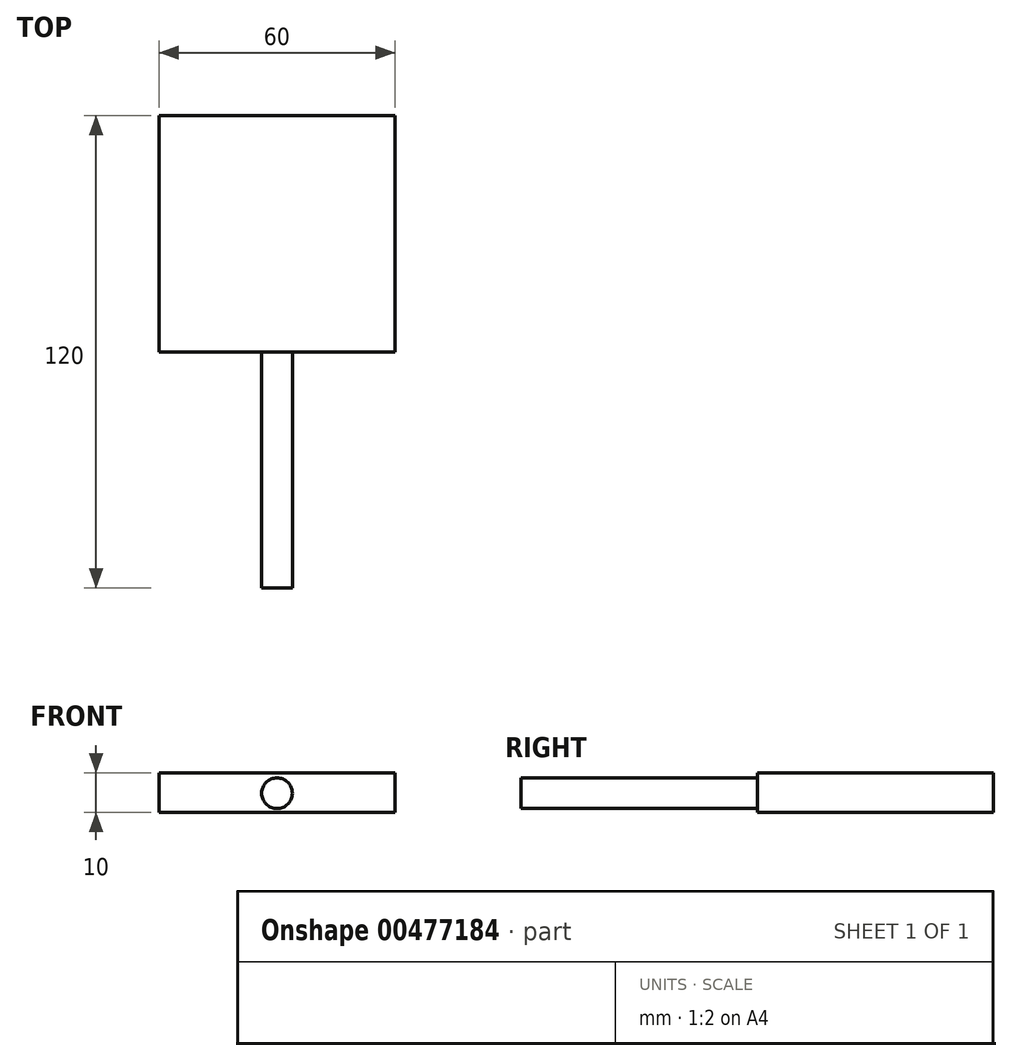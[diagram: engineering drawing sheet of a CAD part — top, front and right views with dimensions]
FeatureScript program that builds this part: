
annotation { "Feature Type Name" : "Feature", "Feature Type Description" : "" }
export const myFeature = defineFeature(function(context is Context, id is Id, definition is map)
    precondition{}
    {
        {
            var Q0;
            Q0=qCreatedBy(makeId("Top.planeOp"),FACE);
            var sketch = newSketch(context, id + "F0", { "sketchPlane" : qUnion([Q0])});
            skLineSegment(sketch, "E0.bottom", {"start": v(30, -30) * mm, "end": v(-30, -30) * mm});
            skLineSegment(sketch, "E0.top", {"start": v(30, 30) * mm, "end": v(-30, 30) * mm});
            skLineSegment(sketch, "E0.left", {"start": v(30, -30) * mm, "end": v(30, 30) * mm});
            skLineSegment(sketch, "E0.right", {"start": v(-30, -30) * mm, "end": v(-30, 30) * mm});
            skPoint(sketch, "E0.middle", {"position": v(0, 0) * mm});
            skSolve(sketch);
        }
        {
            var Q0;
            Q0=makeQuery(id+"F0.imprint","IMPRINT",FACE,{"disambiguationData":[TD([[makeQuery(id+"F0.imprint","IMPRINT",EDGE,{"derivedFrom":sQuery(id+"F0.wireOp",EDGE,"E0.bottom")}),-1.0]])]});
            extrude(context, id + "F1", {"entities" : qUnion([Q0]), "depth" : 10 * mm});
        }
        {
            var Q0;
            Q0=makeQuery(id+"F1.opExtrude","SWEPT_FACE",FACE,{"disambiguationData":[OSD([sQuery(id+"F0.wireOp",EDGE,"E0.bottom")])]});
            var sketch = newSketch(context, id + "F2", { "sketchPlane" : qUnion([Q0])});
            skCircle(sketch, "E1", {"center": v(0, 4.85) * mm, "radius": 3.89 * mm});
            skPoint(sketch, "E1.centerSnap0", {"position": v(0, 10) * mm});
            skSolve(sketch);
        }
        {
            var Q0;
            Q0 = qSketchRegion(id + "F2", true);
            extrude(context, id + "F3", {"entities" : qUnion([Q0]), "operationType" : NewBodyOperationType.ADD, "depth" : 60 * mm});
        }
    });
